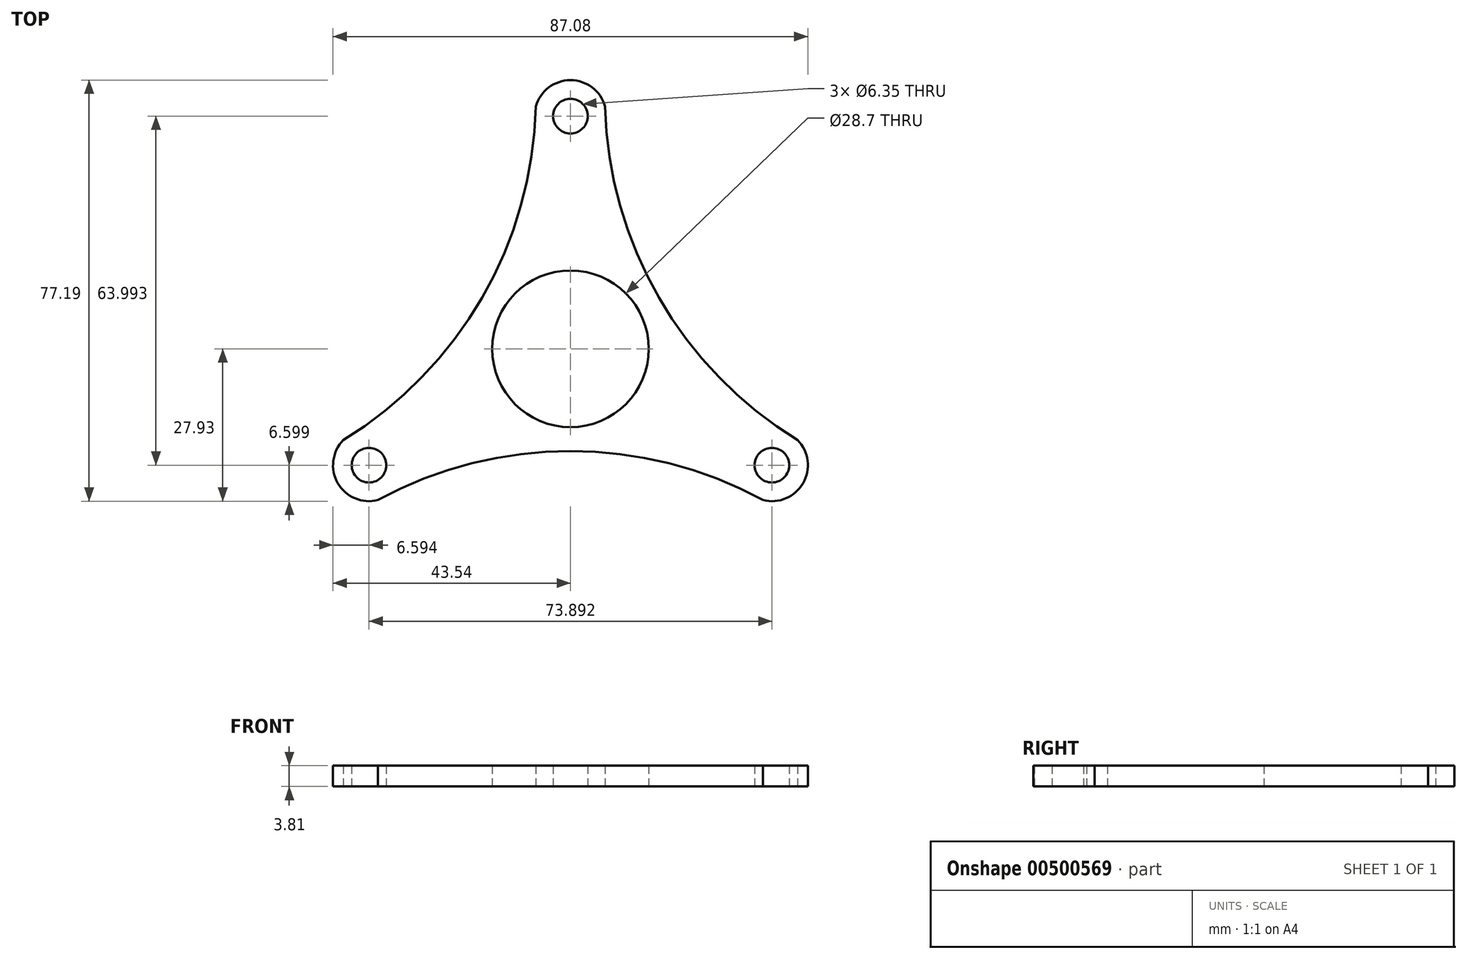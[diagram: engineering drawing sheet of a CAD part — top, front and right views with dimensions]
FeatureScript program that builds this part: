
annotation { "Feature Type Name" : "Feature", "Feature Type Description" : "" }
export const myFeature = defineFeature(function(context is Context, id is Id, definition is map)
    precondition{}
    {
        {
            var Q0;
            Q0=qCreatedBy(makeId("Top.planeOp"),FACE);
            var sketch = newSketch(context, id + "F0", { "sketchPlane" : qUnion([Q0])});
            skCircle(sketch, "E0", {"center": v(0, 0) * mm, "radius": 14.35 * mm});
            skArc(sketch, "E1", {"start": v(6.35, 44.45) * mm, "mid": v(0, 49.26) * mm, "end": v(-6.35, 44.45) * mm});
            skArc(sketch, "E2", {"start": v(-41.67, -16.73) * mm, "mid": v(-42.66, -24.63) * mm, "end": v(-35.32, -27.72) * mm});
            skArc(sketch, "E3", {"start": v(35.32, -27.72) * mm, "mid": v(42.66, -24.63) * mm, "end": v(41.67, -16.73) * mm});
            skArc(sketch, "E4", {"start": v(-41.67, -16.73) * mm, "mid": v(-16.23, 9.37) * mm, "end": v(-6.35, 44.45) * mm});
            skArc(sketch, "E5", {"start": v(6.35, 44.45) * mm, "mid": v(16.23, 9.37) * mm, "end": v(41.67, -16.73) * mm});
            skArc(sketch, "E6", {"start": v(35.32, -27.72) * mm, "mid": v(0, -18.74) * mm, "end": v(-35.32, -27.72) * mm});
            skCircle(sketch, "E7", {"center": v(-36.95, -21.33) * mm, "radius": 3.18 * mm});
            skCircle(sketch, "E8", {"center": v(36.95, -21.33) * mm, "radius": 3.18 * mm});
            skCircle(sketch, "E9", {"center": v(0, 42.66) * mm, "radius": 3.18 * mm});
            skSolve(sketch);
        }
        {
            var Q0;
            Q0=makeQuery(id+"F0.imprint","IMPRINT",FACE,{"disambiguationData":[TD([[makeQuery(id+"F0.imprint","IMPRINT",EDGE,{"derivedFrom":sQuery(id+"F0.wireOp",EDGE,"E0")}),-1.0]])]});
            extrude(context, id + "F1", {"entities" : qUnion([Q0]), "depth" : 3.8 * mm});
        }
    });
